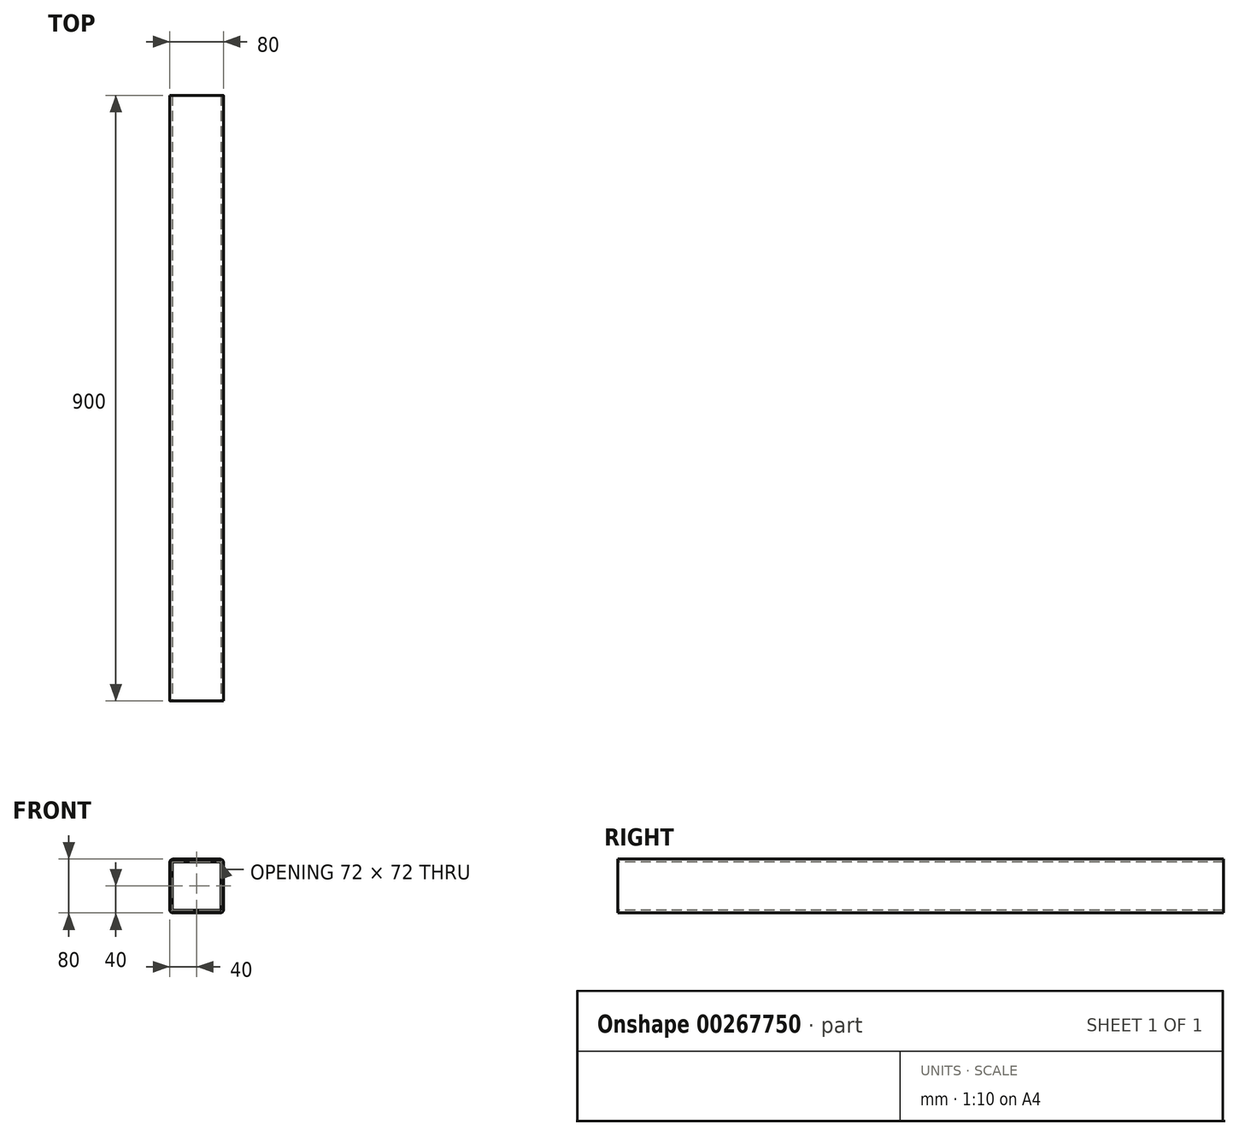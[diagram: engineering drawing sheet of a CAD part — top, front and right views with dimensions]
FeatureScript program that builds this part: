
annotation { "Feature Type Name" : "Feature", "Feature Type Description" : "" }
export const myFeature = defineFeature(function(context is Context, id is Id, definition is map)
    precondition{}
    {
        {
            var Q0;
            Q0=qCreatedBy(makeId("Front.planeOp"),FACE);
            var sketch = newSketch(context, id + "F0", { "sketchPlane" : qUnion([Q0])});
            skLineSegment(sketch, "E0.bottom", {"start": v(35, 40) * mm, "end": v(-35, 40) * mm});
            skLineSegment(sketch, "E0.top", {"start": v(35, -40) * mm, "end": v(-35, -40) * mm});
            skLineSegment(sketch, "E0.left", {"start": v(40, 35) * mm, "end": v(40, -35) * mm});
            skLineSegment(sketch, "E0.right", {"start": v(-40, 35) * mm, "end": v(-40, -35) * mm});
            skPoint(sketch, "E0.middle", {"position": v(0, 0) * mm});
            skPoint(sketch, "E1.visualSharp", {"position": v(-40, 40) * mm});
            skArc(sketch, "E1.filletArc", {"start": v(-35, 40) * mm, "mid": v(-38.54, 38.54) * mm, "end": v(-40, 35) * mm});
            skPoint(sketch, "E2.visualSharp", {"position": v(40, 40) * mm});
            skArc(sketch, "E2.filletArc", {"start": v(40, 35) * mm, "mid": v(38.54, 38.54) * mm, "end": v(35, 40) * mm});
            skPoint(sketch, "E3.visualSharp", {"position": v(40, -40) * mm});
            skArc(sketch, "E3.filletArc", {"start": v(35, -40) * mm, "mid": v(38.54, -38.54) * mm, "end": v(40, -35) * mm});
            skPoint(sketch, "E4.visualSharp", {"position": v(-40, -40) * mm});
            skArc(sketch, "E4.filletArc", {"start": v(-40, -35) * mm, "mid": v(-38.54, -38.54) * mm, "end": v(-35, -40) * mm});
            skArc(sketch, "E5.0", {"start": v(-35, 36) * mm, "mid": v(-35.7, 35.7) * mm, "end": v(-36, 35) * mm});
            skLineSegment(sketch, "E5.1", {"start": v(35, 36) * mm, "end": v(-35, 36) * mm});
            skLineSegment(sketch, "E5.2", {"start": v(-36, 35) * mm, "end": v(-36, -35) * mm});
            skArc(sketch, "E5.3", {"start": v(36, 35) * mm, "mid": v(35.7, 35.7) * mm, "end": v(35, 36) * mm});
            skArc(sketch, "E5.4", {"start": v(-36, -35) * mm, "mid": v(-35.7, -35.7) * mm, "end": v(-35, -36) * mm});
            skLineSegment(sketch, "E5.5", {"start": v(35, -36) * mm, "end": v(-35, -36) * mm});
            skArc(sketch, "E5.6", {"start": v(35, -36) * mm, "mid": v(35.7, -35.7) * mm, "end": v(36, -35) * mm});
            skLineSegment(sketch, "E5.7", {"start": v(36, 35) * mm, "end": v(36, -35) * mm});
            skSolve(sketch);
        }
        {
            var Q0;
            Q0=makeQuery(id+"F0.imprint","IMPRINT",FACE,{"disambiguationData":[TD([[makeQuery(id+"F0.imprint","IMPRINT",EDGE,{"derivedFrom":sQuery(id+"F0.wireOp",EDGE,"E0.bottom")}),1.0]])]});
            extrude(context, id + "F1", {"entities" : qUnion([Q0]), "oppositeDirection" : true, "depth" : 900 * mm});
        }
    });
